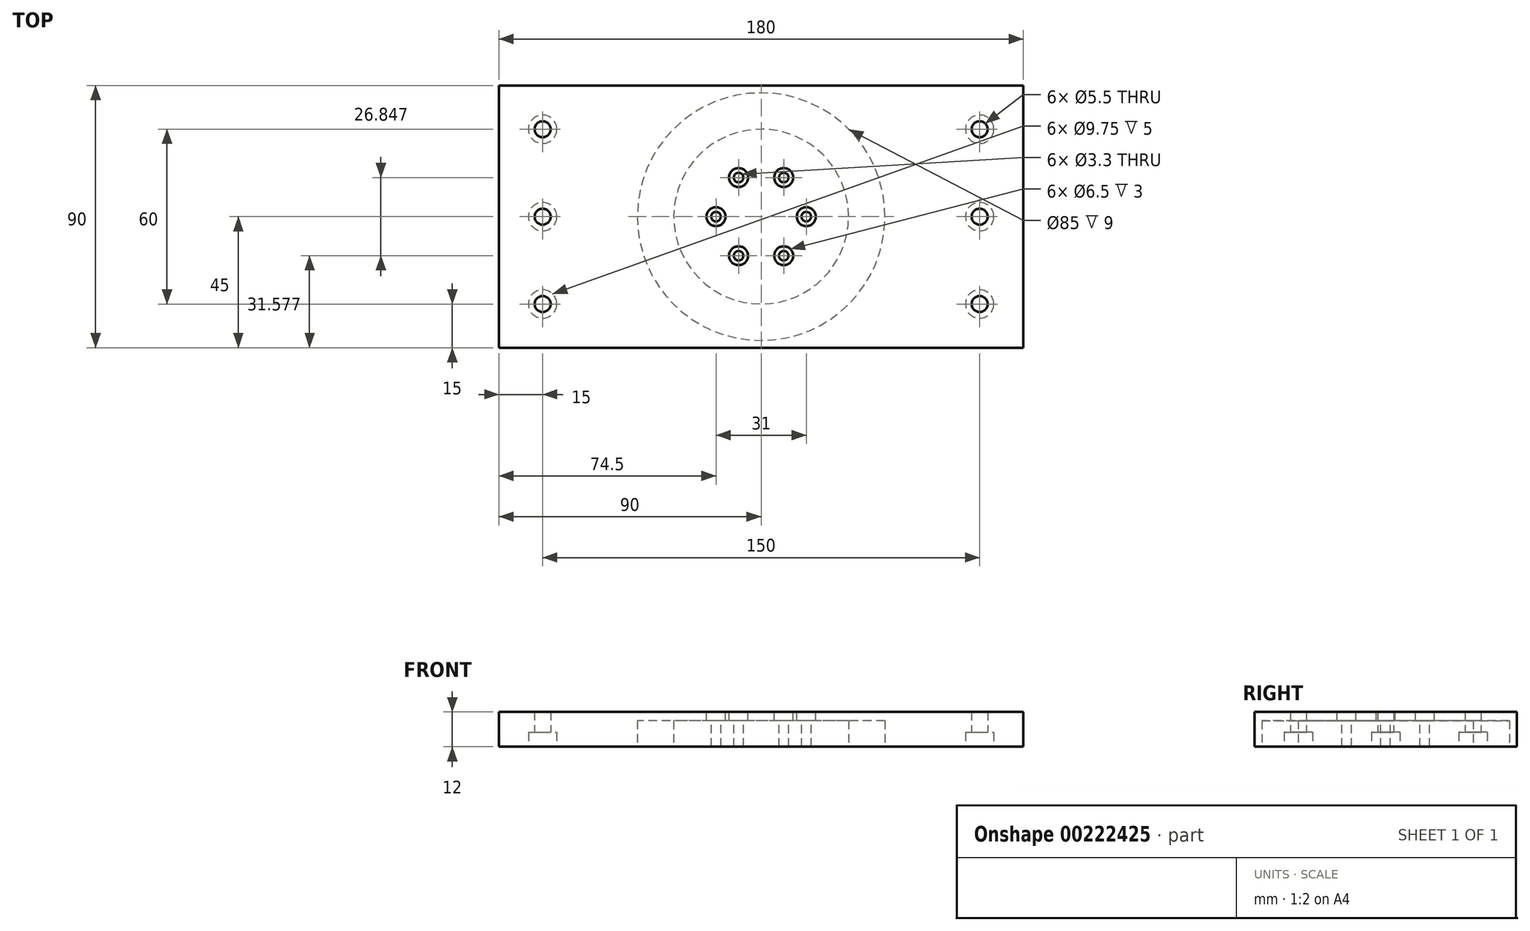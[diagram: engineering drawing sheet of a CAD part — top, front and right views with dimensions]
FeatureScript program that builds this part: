
annotation { "Feature Type Name" : "Feature", "Feature Type Description" : "" }
export const myFeature = defineFeature(function(context is Context, id is Id, definition is map)
    precondition{}
    {
        {
            var Q0;
            Q0=qCreatedBy(makeId("Top.planeOp"),FACE);
            var sketch = newSketch(context, id + "F0", { "sketchPlane" : qUnion([Q0])});
            skLineSegment(sketch, "E0.bottom", {"start": v(-90, -45) * mm, "end": v(90, -45) * mm});
            skLineSegment(sketch, "E0.top", {"start": v(-90, 45) * mm, "end": v(90, 45) * mm});
            skLineSegment(sketch, "E0.left", {"start": v(-90, -45) * mm, "end": v(-90, 45) * mm});
            skLineSegment(sketch, "E0.right", {"start": v(90, -45) * mm, "end": v(90, 45) * mm});
            skPoint(sketch, "E1", {"position": v(-75, -30) * mm});
            skLineSegment(sketch, "E2", {"start": v(-90, 0) * mm, "end": v(90, 0) * mm, "construction": true});
            skLineSegment(sketch, "E3", {"start": v(0, 45) * mm, "end": v(0, -45) * mm, "construction": true});
            skPoint(sketch, "E4.0.1.0", {"position": v(-75, 0) * mm});
            skPoint(sketch, "E4.0.2.0", {"position": v(-75, 30) * mm});
            skLineSegment(sketch, "E4.direction1", {"start": v(-75, -30) * mm, "end": v(-50, -30) * mm, "construction": true});
            skLineSegment(sketch, "E4.direction2", {"start": v(-75, -30) * mm, "end": v(-75, 0) * mm, "construction": true});
            skPoint(sketch, "E5.MirrorP", {"position": v(75, -30) * mm});
            skPoint(sketch, "E6.MirrorP", {"position": v(75, 0) * mm});
            skPoint(sketch, "E7.MirrorP", {"position": v(75, 30) * mm});
            skCircle(sketch, "E8", {"center": v(0, 0) * mm, "radius": 42.5 * mm});
            skPoint(sketch, "E9", {"position": v(15.5, 0) * mm});
            skPoint(sketch, "E10.1.0", {"position": v(7.75, 13.42) * mm});
            skPoint(sketch, "E10.2.0", {"position": v(-7.75, 13.42) * mm});
            skPoint(sketch, "E11.0.3.0", {"position": v(-15.5, 0) * mm});
            skPoint(sketch, "E11.0.4.0", {"position": v(-7.75, -13.42) * mm});
            skPoint(sketch, "E11.0.5.0", {"position": v(7.75, -13.42) * mm});
            skCircle(sketch, "E12", {"center": v(0, 0) * mm, "radius": 30 * mm});
            skSolve(sketch);
        }
        {
            var Q0;
            Q0=makeQuery(id+"F0.imprint","IMPRINT",FACE,{"disambiguationData":[TD([[makeQuery(id+"F0.imprint","IMPRINT",EDGE,{"derivedFrom":sQuery(id+"F0.wireOp",EDGE,"E0.bottom")}),1.0]])]});
            var Q1;
            Q1=makeQuery(id+"F0.imprint","IMPRINT",FACE,{"disambiguationData":[TD([[makeQuery(id+"F0.imprint","IMPRINT",EDGE,{"derivedFrom":sQuery(id+"F0.wireOp",EDGE,"E12")}),1.0]])]});
            var Q2;
            Q2=makeQuery(id+"F0.imprint","IMPRINT",FACE,{"disambiguationData":[TD([[makeQuery(id+"F0.imprint","IMPRINT",EDGE,{"derivedFrom":sQuery(id+"F0.wireOp",EDGE,"E8")}),1.0]])]});
            extrude(context, id + "F1", {"entities" : qUnion([Q0, Q1, Q2]), "depth" : 12 * mm});
        }
        {
            var Q0;
            Q0=sQuery(id+"F0.wireOp",VERTEX,"E5.MirrorP");
            var Q1;
            Q1=sQuery(id+"F0.wireOp",VERTEX,"E6.MirrorP");
            var Q2;
            Q2=sQuery(id+"F0.wireOp",VERTEX,"E7.MirrorP");
            var Q3;
            Q3=sQuery(id+"F0.wireOp",VERTEX,"E4.0.2.0");
            var Q4;
            Q4=sQuery(id+"F0.wireOp",VERTEX,"E4.0.1.0");
            var Q5;
            Q5=sQuery(id+"F0.wireOp",VERTEX,"E1");
            var Q6;
            Q6=makeQuery(id+"F1.opExtrude","SWEPT_BODY",BODY,{"disambiguationData":[OSD([sQuery(id+"F0.wireOp",EDGE,"E0.bottom"),sQuery(id+"F0.wireOp",EDGE,"E0.top"),sQuery(id+"F0.wireOp",EDGE,"E0.left"),sQuery(id+"F0.wireOp",EDGE,"E0.right")])]});
            hole(context, id + "F2", {"style" : HoleStyle.C_BORE, "endStyle" : HoleEndStyle.THROUGH, "oppositeDirection" : true, "standardTappedOrClearance" : lookupTablePath({ "standard" : "ISO", "fit" : "Normal", "size" : "M5", "type" : "Clearance" }), "standardBlindInLast" : lookupTablePath({ "fit" : "Standard", "standard" : "ISO", "size" : "M5", "type" : "Clearance" }), "holeDiameter" : 5.5 * mm, "cBoreDiameter" : 9.75 * mm, "cBoreDepth" : 5 * mm, "locations" : qUnion([Q0, Q1, Q2, Q3, Q4, Q5]), "scope" : qUnion([Q6]), "isTappedThrough" : true});
        }
        {
            var Q0;
            Q0=makeQuery(id+"F1.opExtrude","CAP_FACE",FACE,{"disambiguationData":[OSD([sQuery(id+"F0.wireOp",EDGE,"E0.bottom"),sQuery(id+"F0.wireOp",EDGE,"E0.top"),sQuery(id+"F0.wireOp",EDGE,"E0.left"),sQuery(id+"F0.wireOp",EDGE,"E0.right")])],"isStart":false});
            var sketch = newSketch(context, id + "F3", { "sketchPlane" : qUnion([Q0])});
            skPoint(sketch, "E13.0", {"position": v(7.75, -13.42) * mm});
            skPoint(sketch, "E13.1", {"position": v(-7.75, -13.42) * mm});
            skPoint(sketch, "E13.2", {"position": v(-15.5, 0) * mm});
            skPoint(sketch, "E13.3", {"position": v(-7.75, 13.42) * mm});
            skPoint(sketch, "E13.4", {"position": v(7.75, 13.42) * mm});
            skPoint(sketch, "E13.5", {"position": v(15.5, 0) * mm});
            skSolve(sketch);
        }
        {
            var Q0;
            Q0=sQuery(id+"F3.wireOp",VERTEX,"E13.2");
            var Q1;
            Q1=sQuery(id+"F3.wireOp",VERTEX,"E13.3");
            var Q2;
            Q2=sQuery(id+"F3.wireOp",VERTEX,"E13.4");
            var Q3;
            Q3=sQuery(id+"F3.wireOp",VERTEX,"E13.5");
            var Q4;
            Q4=sQuery(id+"F3.wireOp",VERTEX,"E13.0");
            var Q5;
            Q5=sQuery(id+"F3.wireOp",VERTEX,"E13.1");
            var Q6;
            Q6=makeQuery(id+"F1.opExtrude","SWEPT_BODY",BODY,{"disambiguationData":[OSD([sQuery(id+"F0.wireOp",EDGE,"E0.bottom"),sQuery(id+"F0.wireOp",EDGE,"E0.top"),sQuery(id+"F0.wireOp",EDGE,"E0.left"),sQuery(id+"F0.wireOp",EDGE,"E0.right")])]});
            hole(context, id + "F4", {"style" : HoleStyle.C_BORE, "endStyle" : HoleEndStyle.THROUGH, "standardTappedOrClearance" : lookupTablePath({ "standard" : "ISO", "fit" : "Normal", "size" : "M3", "type" : "Clearance" }), "standardBlindInLast" : lookupTablePath({ "fit" : "Standard", "standard" : "ISO", "size" : "M3", "type" : "Clearance" }), "holeDiameter" : 3.3 * mm, "cBoreDiameter" : 6.5 * mm, "cBoreDepth" : 3 * mm, "locations" : qUnion([Q0, Q1, Q2, Q3, Q4, Q5]), "scope" : qUnion([Q6]), "isTappedThrough" : true});
        }
        {
            var Q0;
            Q0=makeQuery(id+"F0.imprint","IMPRINT",FACE,{"disambiguationData":[TD([[makeQuery(id+"F0.imprint","IMPRINT",EDGE,{"derivedFrom":sQuery(id+"F0.wireOp",EDGE,"E8")}),1.0]])]});
            extrude(context, id + "F5", {"entities" : qUnion([Q0]), "operationType" : NewBodyOperationType.REMOVE, "depth" : 9 * mm});
        }
    });
